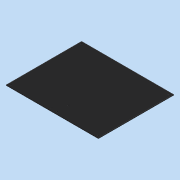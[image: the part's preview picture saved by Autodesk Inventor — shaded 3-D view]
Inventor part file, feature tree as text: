
AUTODESK INVENTOR PART (.ipt)
format: ipt  version: 2016 (Build 200138000, 138)  size: 109,568 bytes
history: native  units: mm
features: hole x9, extrude x1, sketch x1
ambient origin geometry x8: Origin, YZ Plane, XZ Plane, XY Plane, X Axis, Y Axis, Z Axis, Center Point
bodies: Solid1 (feature_tree)
feature tree (11):
  extrude  "Extrusion1"  Depth=360.0mm
  hole  "Hole1"  [1 undecoded]
  hole  "Hole2"  [1 undecoded]
  hole  "Hole3"  [1 undecoded]
  hole  "Hole4"  [1 undecoded]
  hole  "Hole5"  [1 undecoded]
  hole  "Hole6"  [1 undecoded]
  hole  "Hole7"  [1 undecoded]
  hole  "Hole8"  [1 undecoded]
  hole  "Hole9"  [1 undecoded]
  sketch  "Sketch1"  dims[d0=440.0mm d1=360.0mm d2=3.0mm d3=0.0mm d4=12.0mm d5=12.0mm d6=4.0mm d7=6.0mm d8=4.0mm d9=2.0mm d10=90.0deg d11=8.0mm d12=20.594885mm d13=12.0mm d14=12.0mm d15=4.0mm d16=6.0mm d17=4.0mm d18=2.0mm d19=90.0deg d20=8.0mm d21=20.594885mm d22=12.0mm d23=12.0mm d24=4.0mm d25=6.0mm d26=4.0mm d27=2.0mm d28=90.0deg d29=8.0mm d30=20.594885mm d31=12.0mm d32=12.0mm d33=4.0mm d34=6.0mm d35=4.0mm d36=2.0mm d37=90.0deg d38=8.0mm d39=20.594885mm d40=12.0mm d41=206.5mm d42=4.0mm d43=6.0mm d44=4.0mm d45=2.0mm d46=90.0deg d47=8.0mm d48=20.594885mm d49=206.5mm d50=12.0mm d51=4.0mm d52=6.0mm d53=4.0mm d54=2.0mm d55=90.0deg d56=8.0mm d57=20.594885mm d58=206.5mm d59=63.0mm d60=4.0mm d61=6.0mm d62=4.0mm d63=2.0mm d64=90.0deg d65=8.0mm d66=20.594885mm d67=12.0mm d68=206.5mm d69=4.0mm d70=6.0mm d71=4.0mm d72=2.0mm d73=90.0deg d74=8.0mm d75=20.594885mm d76=12.0mm d77=206.5mm d78=4.0mm d79=6.0mm d80=4.0mm d81=2.0mm d82=90.0deg d83=8.0mm d84=20.594885mm]
note: 9 required parameter values undecoded (feature->parameter linkage not recoverable at this tier; creation-order binding heuristic only, values carry confidence <= 0.55)
